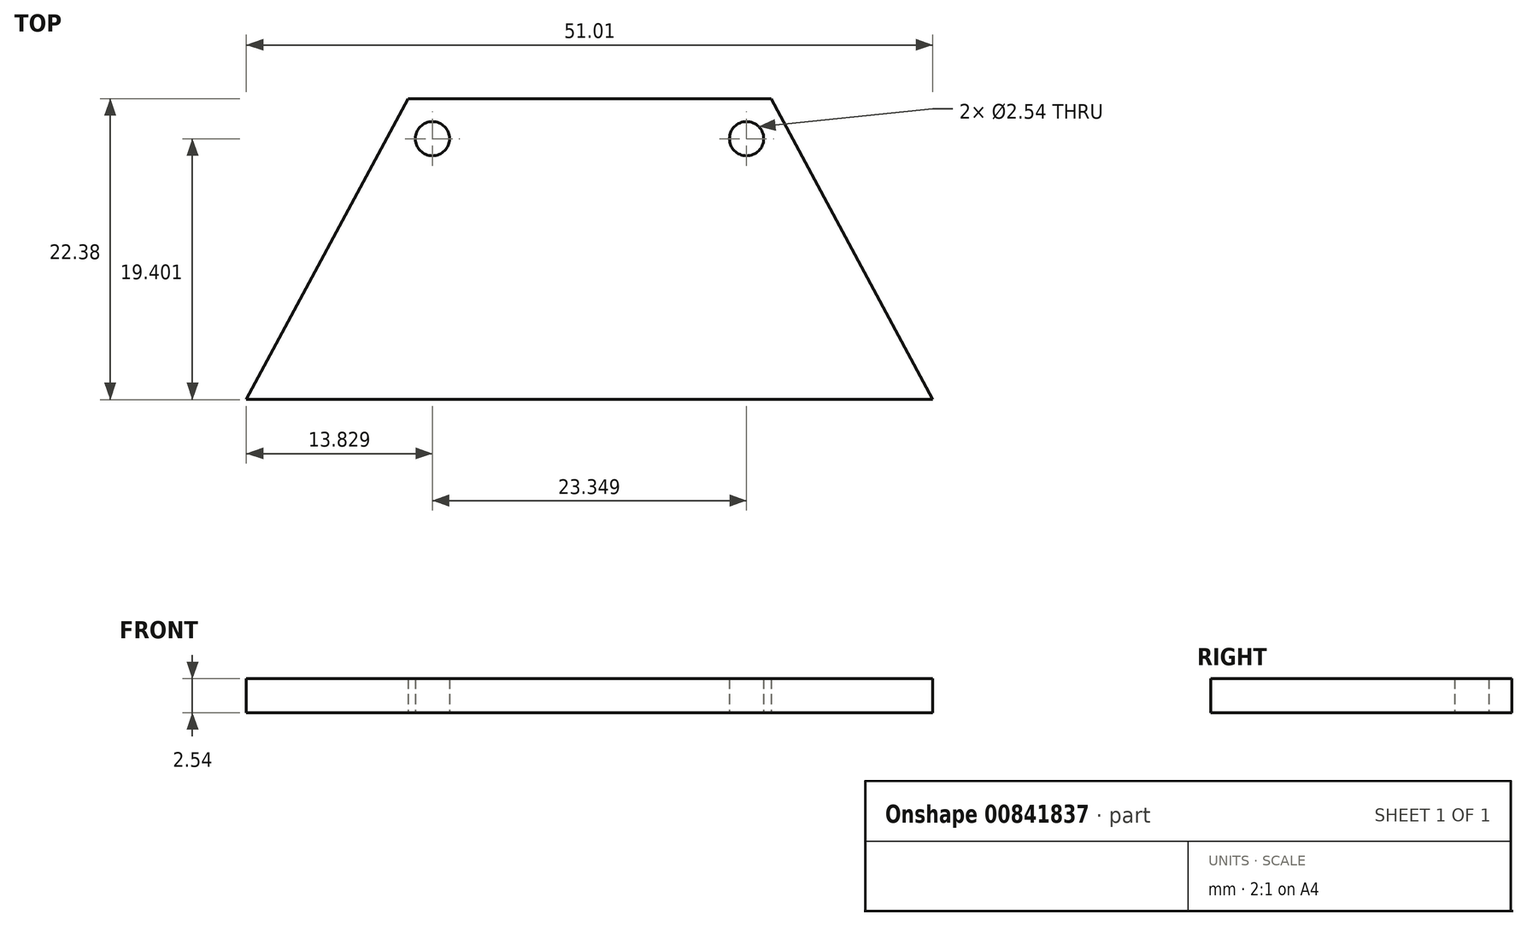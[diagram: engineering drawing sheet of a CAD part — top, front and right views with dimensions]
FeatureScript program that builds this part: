
annotation { "Feature Type Name" : "Feature", "Feature Type Description" : "" }
export const myFeature = defineFeature(function(context is Context, id is Id, definition is map)
    precondition{}
    {
        {
            var Q0;
            Q0=qCreatedBy(makeId("Top.planeOp"),FACE);
            var sketch = newSketch(context, id + "F0", { "sketchPlane" : qUnion([Q0])});
            skLineSegment(sketch, "E0", {"start": v(-21.22, -5.58) * mm, "end": v(29.79, -5.58) * mm});
            skLineSegment(sketch, "E1", {"start": v(-9.2, 16.8) * mm, "end": v(17.78, 16.8) * mm});
            skLineSegment(sketch, "E2", {"start": v(-9.2, 16.8) * mm, "end": v(-21.22, -5.58) * mm});
            skLineSegment(sketch, "E3", {"start": v(17.78, 16.8) * mm, "end": v(29.79, -5.58) * mm});
            skCircle(sketch, "E4", {"center": v(-7.4, 13.82) * mm, "radius": 1.27 * mm});
            skCircle(sketch, "E5", {"center": v(15.96, 13.82) * mm, "radius": 1.27 * mm});
            skSolve(sketch);
        }
        {
            var Q0;
            Q0=makeQuery(id+"F0.imprint","IMPRINT",FACE,{"disambiguationData":[TD([[makeQuery(id+"F0.imprint","IMPRINT",EDGE,{"derivedFrom":sQuery(id+"F0.wireOp",EDGE,"E0")}),1.0]])]});
            extrude(context, id + "F1", {"entities" : qUnion([Q0]), "depth" : 2.54 * mm, "offsetDistance" : 25.4 * mm});
        }
    });
